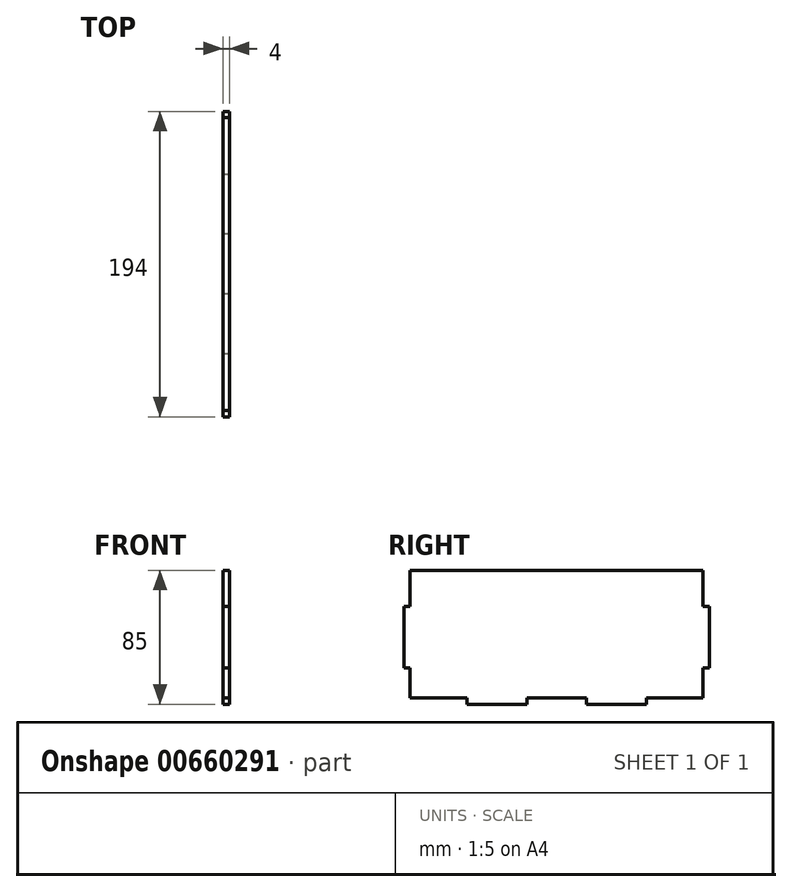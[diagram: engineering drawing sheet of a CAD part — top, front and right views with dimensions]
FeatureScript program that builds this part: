
annotation { "Feature Type Name" : "Feature", "Feature Type Description" : "" }
export const myFeature = defineFeature(function(context is Context, id is Id, definition is map)
    precondition{}
    {
        {
            var Q0;
            Q0=qCreatedBy(makeId("Right.planeOp"),FACE);
            var sketch = newSketch(context, id + "F0", { "sketchPlane" : qUnion([Q0])});
            skLineSegment(sketch, "E0.bottom", {"start": v(0, 0) * mm, "end": v(194, 0) * mm});
            skLineSegment(sketch, "E0.top", {"start": v(0, 85) * mm, "end": v(194, 85) * mm});
            skLineSegment(sketch, "E0.left", {"start": v(0, 0) * mm, "end": v(0, 85) * mm});
            skLineSegment(sketch, "E0.right", {"start": v(194, 0) * mm, "end": v(194, 85) * mm});
            skLineSegment(sketch, "E1.bottom", {"start": v(0, 85) * mm, "end": v(4, 85) * mm});
            skLineSegment(sketch, "E1.top", {"start": v(0, 62) * mm, "end": v(4, 62) * mm});
            skLineSegment(sketch, "E1.left", {"start": v(0, 85) * mm, "end": v(0, 62) * mm});
            skLineSegment(sketch, "E1.right", {"start": v(4, 85) * mm, "end": v(4, 62) * mm});
            skLineSegment(sketch, "E2.bottom", {"start": v(0, 0) * mm, "end": v(4, 0) * mm});
            skLineSegment(sketch, "E2.top", {"start": v(0, 23) * mm, "end": v(4, 23) * mm});
            skLineSegment(sketch, "E2.left", {"start": v(0, 0) * mm, "end": v(0, 23) * mm});
            skLineSegment(sketch, "E2.right", {"start": v(4, 0) * mm, "end": v(4, 23) * mm});
            skLineSegment(sketch, "E3.top", {"start": v(194, 62) * mm, "end": v(190, 62) * mm});
            skLineSegment(sketch, "E3.left", {"start": v(194, 85) * mm, "end": v(194, 62) * mm});
            skLineSegment(sketch, "E3.right", {"start": v(190, 85) * mm, "end": v(190, 62) * mm});
            skLineSegment(sketch, "E4.bottom", {"start": v(194, 0) * mm, "end": v(190, 0) * mm});
            skLineSegment(sketch, "E4.top", {"start": v(194, 23) * mm, "end": v(190, 23) * mm});
            skLineSegment(sketch, "E4.left", {"start": v(194, 0) * mm, "end": v(194, 23) * mm});
            skLineSegment(sketch, "E4.right", {"start": v(190, 0) * mm, "end": v(190, 23) * mm});
            skLineSegment(sketch, "E5.bottom", {"start": v(0, 0) * mm, "end": v(40, 0) * mm});
            skLineSegment(sketch, "E5.top", {"start": v(0, 4) * mm, "end": v(40, 4) * mm});
            skLineSegment(sketch, "E5.left", {"start": v(0, 0) * mm, "end": v(0, 4) * mm});
            skLineSegment(sketch, "E5.right", {"start": v(40, 0) * mm, "end": v(40, 4) * mm});
            skLineSegment(sketch, "E6.bottom", {"start": v(78, 0) * mm, "end": v(116, 0) * mm});
            skLineSegment(sketch, "E6.top", {"start": v(78, 4) * mm, "end": v(116, 4) * mm});
            skLineSegment(sketch, "E6.left", {"start": v(78, 0) * mm, "end": v(78, 4) * mm});
            skLineSegment(sketch, "E6.right", {"start": v(116, 0) * mm, "end": v(116, 4) * mm});
            skLineSegment(sketch, "E7.bottom", {"start": v(194, 0) * mm, "end": v(154, 0) * mm});
            skLineSegment(sketch, "E7.top", {"start": v(194, 4) * mm, "end": v(154, 4) * mm});
            skLineSegment(sketch, "E7.left", {"start": v(194, 0) * mm, "end": v(194, 4) * mm});
            skLineSegment(sketch, "E7.right", {"start": v(154, 0) * mm, "end": v(154, 4) * mm});
            skSolve(sketch);
        }
        {
            var Q0;
            {var subQ12=sQuery(id+"F0.wireOp",EDGE,"E1.top");Q0=makeQuery(id+"F0.imprint","IMPRINT",FACE,{"disambiguationData":[TD([[makeQuery(id+"F0.imprint","IMPRINT",EDGE,{"derivedFrom":subQ12}),-1.0]])]});}
            extrude(context, id + "F1", {"entities" : qUnion([Q0]), "depth" : 4 * mm, "offsetDistance" : 25 * mm});
        }
    });
